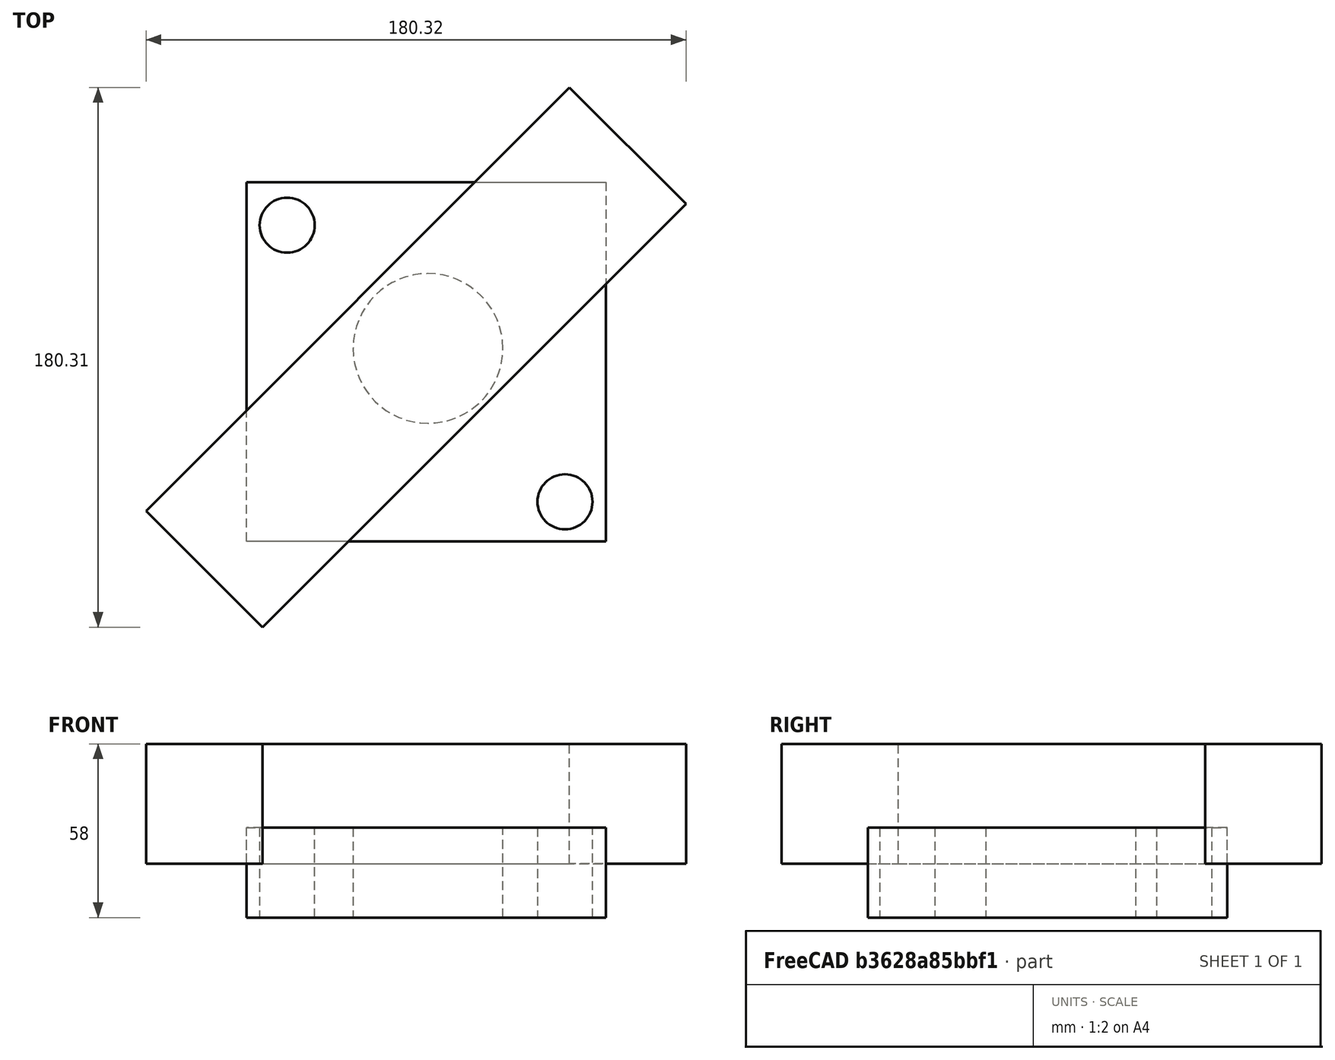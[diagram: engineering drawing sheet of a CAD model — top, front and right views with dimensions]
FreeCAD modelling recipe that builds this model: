
FCSTD DOCUMENT  (FreeCAD 0.18R16131 (Git))
Label: Momentum_Middle
License: All rights reserved
LicenseURL: http://en.wikipedia.org/wiki/All_rights_reserved
objects: Sketcher::SketchObject×1, Part::Extrusion×1, Part::Box×1
note: 3 computed .brp shape members not serialized (recipe doc carries the construction recipe); baked Part::Feature solids carry a one-line shape summary decoded from their .brp

FEATURE [Sketcher::SketchObject] Sketch
  sketch-geometry (7):
    g0: LineSegment StartX=-66.9458 StartY=62.3125 StartZ=0 EndX=53.0542 EndY=62.3125 EndZ=0
    g1: LineSegment StartX=53.0542 StartY=62.3125 StartZ=0 EndX=53.0542 EndY=-57.6875 EndZ=0
    g2: LineSegment StartX=53.0542 StartY=-57.6875 StartZ=0 EndX=-66.9458 EndY=-57.6875 EndZ=0
    g3: LineSegment StartX=-66.9458 StartY=-57.6875 StartZ=0 EndX=-66.9458 EndY=62.3125 EndZ=0
    g4: Circle CenterX=-53.3461 CenterY=47.9303 CenterZ=0 NormalX=0 NormalY=0 NormalZ=1 AngleXU=0 Radius=9.191
    g5: Circle CenterX=39.4455 CenterY=-44.5002 CenterZ=0 NormalX=0 NormalY=0 NormalZ=1 AngleXU=0 Radius=9.191
    g6: Circle CenterX=-6.30312 CenterY=6.74399 CenterZ=0 NormalX=0 NormalY=0 NormalZ=1 AngleXU=0 Radius=25
  constraints (11):
    c: Coincident(g0,g1)
    c: Coincident(g1,g2)
    c: Coincident(g2,g3)
    c: Coincident(g3,g0)
    c: Horizontal(g0)
    c: Horizontal(g2)
    c: Vertical(g1)
    c: Vertical(g3)
    c: DistanceY(g3,g3) = 120
    c: DistanceX(g0,g0) = 120
    c: Radius(g6) = 25
FEATURE [Part::Extrusion] Extrude001
  Base = -> Sketch
  Dir = (0,0,1)
  DirMode = 2
  FaceMakerClass = Part::FaceMakerBullseye
  LengthFwd = 30
  LengthRev = 0
  Solid = true
  Symmetric = false
FEATURE [Part::Box] Box  label="Cube"
  AttacherType = Attacher::AttachEngine3D
  Height = 40
  Length = 200
  Placement = pos=(-61.5858,-86.4142,18) rot=(0,0,1;0.785398rad)
  Width = 55
